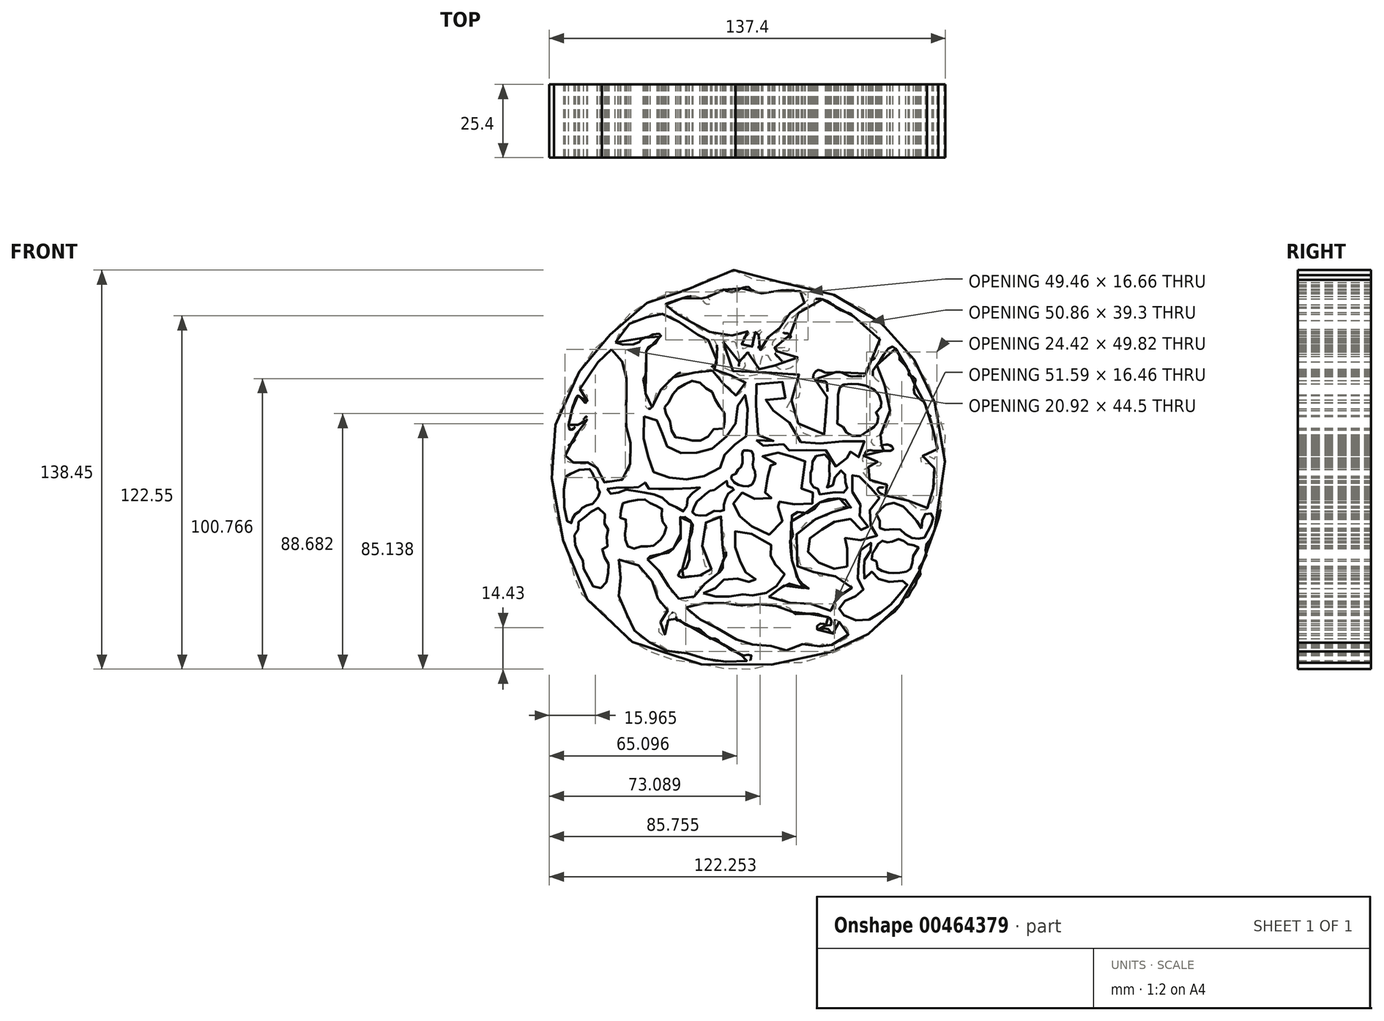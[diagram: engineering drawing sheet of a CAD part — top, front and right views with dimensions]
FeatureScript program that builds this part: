
annotation { "Feature Type Name" : "Feature", "Feature Type Description" : "" }
export const myFeature = defineFeature(function(context is Context, id is Id, definition is map)
    precondition{}
    {
        {
            var Q0;
            Q0=qCreatedBy(makeId("Front.planeOp"),FACE);
            var sketch = newSketch(context, id + "F0", { "sketchPlane" : qUnion([Q0])});
            skFitSpline(sketch, "E0", {"points": [v(-58.3, 41.66) * mm, v(-56.87, 40.83) * mm, v(-56.04, 38.93) * mm, v(-54.73, 37.5) * mm, v(-53.54, 36.31) * mm, v(-53.19, 34.05) * mm, v(-53.07, 31.2) * mm, v(-53.19, 15.04) * mm, v(-52.35, 14.2) * mm, v(-52.23, 11.47) * mm, v(-51.64, 9.21) * mm, v(-51.52, 6.96) * mm, v(-51.64, 3.75) * mm, v(-52.12, 0) * mm, v(-53.07, -2.2) * mm, v(-54.02, -3.38) * mm, v(-56.63, -3.86) * mm, v(-58.65, -3.98) * mm, v(-60.55, -4.45) * mm, v(-61.39, -4.1) * mm, v(-61.86, -2.55) * mm, v(-63.05, 0) * mm, v(-64, 1.6) * mm, v(-64.83, 2.8) * mm, v(-65.55, 3.27) * mm, v(-66.5, 2.44) * mm, v(-67.45, 1.85) * mm, v(-68.64, 1.73) * mm, v(-70.66, 2.08) * mm, v(-71.84, 2.44) * mm, v(-73.4, 2.32) * mm, v(-74.34, 2.56) * mm, v(-74.34, 4.46) * mm, v(-74.34, 6.48) * mm, v(-74.22, 8.03) * mm, v(-73.03, 8.5) * mm, v(-71.49, 9.69) * mm, v(-70.78, 10.88) * mm, v(-70.9, 12.42) * mm, v(-69.7, 13.14) * mm, v(-68.4, 13.73) * mm, v(-67.33, 15.28) * mm, v(-66.85, 16.7) * mm, v(-66.97, 18.37) * mm, v(-67.92, 17.41) * mm, v(-69.23, 15.99) * mm, v(-70.66, 15.04) * mm, v(-71.6, 13.97) * mm, v(-72.68, 13.85) * mm, v(-73.15, 15.28) * mm, v(-72.8, 17.06) * mm, v(-72.44, 18.37) * mm, v(-72.08, 20.15) * mm, v(-71.84, 21.57) * mm, v(-71.13, 23.24) * mm, v(-70.66, 24.66) * mm, v(-69.82, 25.62) * mm, v(-68.75, 24.78) * mm, v(-67.92, 23.6) * mm, v(-66.97, 23.12) * mm, v(-66.62, 25.14) * mm, v(-67.1, 26.57) * mm, v(-67.92, 27.52) * mm, v(-69.23, 28) * mm, v(-69.11, 29.18) * mm, v(-68.04, 30.01) * mm, v(-66.73, 31.68) * mm, v(-65.43, 33.46) * mm, v(-64, 35.48) * mm, v(-63.17, 36.9) * mm, v(-61.86, 38.33) * mm, v(-60.55, 39.76) * mm, v(-58.3, 41.66) * mm]});
            skFitSpline(sketch, "E1", {"points": [v(-56.85, 44.1) * mm, v(-49.42, 43.75) * mm, v(-48.22, 44.83) * mm, v(-46.66, 45.79) * mm, v(-45.1, 46.15) * mm, v(-43.42, 46.99) * mm, v(-41.03, 46.75) * mm, v(-42.23, 45.19) * mm, v(-43.3, 43.5) * mm, v(-44.74, 42.9) * mm, v(-46.06, 41.66) * mm, v(-46.18, 39.76) * mm, v(-46.18, 38.11) * mm, v(-46.18, 35.72) * mm, v(-46.66, 32.24) * mm, v(-47.26, 31.16) * mm, v(-46.9, 29.84) * mm, v(-46.66, 27.8) * mm, v(-46.42, 24.57) * mm, v(-46.42, 21.93) * mm, v(-45.46, 21.09) * mm, v(-44.5, 21.33) * mm, v(-43.66, 22.65) * mm, v(-43.18, 25.05) * mm, v(-42.7, 26.36) * mm, v(-41.27, 27.68) * mm, v(-39.83, 27.92) * mm, v(-38.99, 29) * mm, v(-38.63, 30.68) * mm, v(-36.83, 32) * mm, v(-34.8, 33.46) * mm, v(-31.68, 33.46) * mm, v(-30, 33.46) * mm, v(-27.87, 34.16) * mm, v(-26.86, 34.58) * mm, v(-25.34, 34.75) * mm, v(-23.9, 34.75) * mm, v(-22.55, 33.46) * mm, v(-21.11, 32.38) * mm, v(-20.35, 31.2) * mm, v(-20.18, 30.18) * mm, v(-19, 29.5) * mm, v(-17.56, 28.5) * mm, v(-16.46, 27.31) * mm, v(-16.04, 25.96) * mm, v(-15.2, 25.7) * mm, v(-14.1, 26.21) * mm, v(-12.74, 27.48) * mm, v(-11.9, 28.24) * mm, v(-11.73, 29.68) * mm, v(-12.07, 30.7) * mm, v(-13.67, 31.11) * mm, v(-15.2, 31.28) * mm, v(-16.3, 31.96) * mm, v(-16.89, 32.8) * mm, v(-18.58, 32.64) * mm, v(-20.6, 33.46) * mm, v(-22.1, 34.3) * mm, v(-22.53, 34.69) * mm, v(-23.01, 35.21) * mm, v(-23.45, 35.74) * mm, v(-22.48, 36.08) * mm, v(-21.81, 36.9) * mm, v(-21.86, 37.33) * mm, v(-21.76, 38.83) * mm, v(-22.11, 44.86) * mm, v(-23.16, 44.77) * mm, v(-24.65, 44.86) * mm, v(-25.6, 43.99) * mm, v(-26.05, 44.86) * mm, v(-26.05, 46.35) * mm, v(-27.62, 46.52) * mm, v(-29.28, 47.3) * mm, v(-31.11, 48.88) * mm, v(-33.9, 50.65) * mm, v(-35.06, 51.35) * mm, v(-36.36, 52.18) * mm, v(-37.78, 53.12) * mm, v(-39.31, 53.71) * mm, v(-41.08, 54.07) * mm, v(-42.73, 54.3) * mm, v(-44.74, 54.3) * mm, v(-44.86, 53.24) * mm, v(-46.63, 52.77) * mm, v(-48.04, 52.3) * mm, v(-49.34, 51.7) * mm, v(-50.87, 51.59) * mm, v(-52.4, 50.17) * mm, v(-54.06, 48.76) * mm, v(-55.6, 46.99) * mm, v(-56.85, 44.1) * mm]});
            skFitSpline(sketch, "E2", {"points": [v(-47.03, 18.43) * mm, v(-47.03, 15.19) * mm, v(-47.03, 12.58) * mm, v(-47.03, 9.21) * mm, v(-46.28, 7.85) * mm, v(-45.78, 5.98) * mm, v(-45.66, 3.36) * mm, v(-45.53, 1.12) * mm, v(-44.04, 0) * mm, v(-43.3, -1.5) * mm, v(-41.05, -2.11) * mm, v(-39.68, -2.86) * mm, v(-37.81, -2.86) * mm, v(-35.82, -3.73) * mm, v(-34.33, -3.73) * mm, v(-32.09, -3.36) * mm, v(-30.97, -2.86) * mm, v(-28.23, -2.49) * mm, v(-26.24, -2.24) * mm, v(-24.25, -2.11) * mm, v(-22.38, 0) * mm, v(-20.48, 0.65) * mm, v(-20, 1.6) * mm, v(-19.94, 2.84) * mm, v(-19.58, 4.15) * mm, v(-19, 5.1) * mm, v(-17.68, 6.23) * mm, v(-16.91, 7.18) * mm, v(-16.08, 8.2) * mm, v(-15.3, 8.73) * mm, v(-14.24, 9.62) * mm, v(-12.57, 10.33) * mm, v(-11.68, 11.05) * mm, v(-11.44, 12.17) * mm, v(-11.2, 13) * mm, v(-11.2, 14.25) * mm, v(-11.38, 15.86) * mm, v(-11.15, 16.75) * mm, v(-10.79, 18) * mm, v(-11.03, 18.77) * mm, v(-11.2, 20.61) * mm, v(-10.85, 21.45) * mm, v(-10.73, 23.05) * mm, v(-10.99, 24.42) * mm, v(-11.66, 25.7) * mm, v(-13.01, 25.7) * mm, v(-14.27, 24.8) * mm, v(-14.46, 23.94) * mm, v(-14.46, 22.1) * mm, v(-14.46, 20.37) * mm, v(-15.2, 18.15) * mm, v(-15.2, 16.03) * mm, v(-15.2, 14.17) * mm, v(-16.57, 13.18) * mm, v(-18.02, 11.73) * mm, v(-19.8, 10.27) * mm, v(-21.65, 8.75) * mm, v(-23.24, 7.43) * mm, v(-24.16, 6.7) * mm, v(-26.4, 6.11) * mm, v(-27.93, 5.91) * mm, v(-29.31, 5.85) * mm, v(-30.64, 5.85) * mm, v(-32.22, 5.78) * mm, v(-34, 5.72) * mm, v(-35.39, 5.72) * mm, v(-36.78, 6.44) * mm, v(-38.3, 7.3) * mm, v(-39.35, 8.42) * mm, v(-40.4, 9.68) * mm, v(-40.54, 10.8) * mm, v(-40.54, 11.99) * mm, v(-40.87, 12.91) * mm, v(-41.6, 13.57) * mm, v(-42.39, 15.49) * mm, v(-42.39, 16.68) * mm, v(-43.25, 18.06) * mm, v(-44.7, 18.8) * mm, v(-46.09, 18.6) * mm, v(-47.03, 18.43) * mm]});
            skFitSpline(sketch, "E3", {"points": [v(-39.87, 21.63) * mm, v(-39.75, 19.62) * mm, v(-38.45, 18.56) * mm, v(-37.74, 14.89) * mm, v(-37.14, 12.91) * mm, v(-35.96, 11.1) * mm, v(-33.48, 10.86) * mm, v(-30.64, 10.15) * mm, v(-28.62, 9.8) * mm, v(-25.9, 10.74) * mm, v(-24.25, 12.05) * mm, v(-22.23, 14.3) * mm, v(-19, 14.41) * mm, v(-19, 16.54) * mm, v(-19, 19.15) * mm, v(-20.22, 21.28) * mm, v(-22, 23.17) * mm, v(-22.7, 25.7) * mm, v(-23.65, 27.2) * mm, v(-25.2, 28.02) * mm, v(-26.85, 29.5) * mm, v(-28.98, 30.74) * mm, v(-31.1, 30.5) * mm, v(-33, 29.5) * mm, v(-35.01, 28.38) * mm, v(-36.67, 26.84) * mm, v(-37.85, 24.24) * mm, v(-39.04, 22.58) * mm, v(-39.87, 21.63) * mm]});
            skFitSpline(sketch, "E4", {"points": [v(-74, -2.4) * mm, v(-73.42, -18.32) * mm, v(-72.14, -18.44) * mm, v(-71.67, -16.58) * mm, v(-70.51, -15.18) * mm, v(-69.12, -14.25) * mm, v(-67.84, -12.74) * mm, v(-65.43, -12.16) * mm, v(-64.23, -11.23) * mm, v(-63.17, -9.72) * mm, v(-62.25, -8.2) * mm, v(-63.17, -6.23) * mm, v(-63.17, -4.02) * mm, v(-64.46, -2.62) * mm, v(-65.43, 0) * mm, v(-66.9, 0) * mm, v(-69, 0) * mm, v(-70.98, -0.88) * mm, v(-72.37, -1.46) * mm, v(-74, -2.4) * mm]});
            skFitSpline(sketch, "E5", {"points": [v(-69.78, -18.13) * mm, v(-69.78, -19.14) * mm, v(-69.82, -20.68) * mm, v(-70.4, -21.47) * mm, v(-70.92, -21.82) * mm, v(-71.18, -23.63) * mm, v(-70.96, -25.6) * mm, v(-70.61, -27.46) * mm, v(-69.86, -28.64) * mm, v(-68.97, -30.31) * mm, v(-68.2, -31.53) * mm, v(-67.98, -32.6) * mm, v(-67.98, -34.04) * mm, v(-67.52, -35.41) * mm, v(-66.38, -37.24) * mm, v(-65.43, -39.82) * mm, v(-64.1, -40.81) * mm, v(-63.17, -41.2) * mm, v(-61.44, -40.96) * mm, v(-60.55, -40.05) * mm, v(-59.91, -38.53) * mm, v(-59.61, -36.86) * mm, v(-59.3, -34.65) * mm, v(-59.15, -33.13) * mm, v(-60, -31.99) * mm, v(-60.55, -30.7) * mm, v(-61.2, -29.4) * mm, v(-61.44, -28.18) * mm, v(-61.36, -27.12) * mm, v(-60.55, -26.97) * mm, v(-59.76, -26.74) * mm, v(-59.91, -24.68) * mm, v(-59.91, -23.09) * mm, v(-59.53, -22.02) * mm, v(-59.38, -20.8) * mm, v(-59.84, -19.82) * mm, v(-60.55, -19.28) * mm, v(-60.55, -17.23) * mm, v(-60.55, -15.7) * mm, v(-61.28, -13.96) * mm, v(-63.17, -13.35) * mm, v(-64.33, -13.8) * mm, v(-65.43, -14.8) * mm, v(-66.6, -15.86) * mm, v(-68.05, -16.85) * mm, v(-69.12, -17.69) * mm, v(-69.78, -18.13) * mm]});
            skFitSpline(sketch, "E6", {"points": [v(-59.76, -6.69) * mm, v(-59.76, -8.1) * mm, v(-58.3, -8.44) * mm, v(-57.14, -8.44) * mm, v(-55.39, -7.77) * mm, v(-53.89, -7.02) * mm, v(-52.3, -7.19) * mm, v(-49.89, -7.52) * mm, v(-48.14, -7.94) * mm, v(-45.8, -8.1) * mm, v(-43.64, -8.6) * mm, v(-41.72, -9.1) * mm, v(-40.14, -10.27) * mm, v(-38.63, -11.52) * mm, v(-37.48, -12.69) * mm, v(-35.82, -13.1) * mm, v(-34.33, -13.77) * mm, v(-33.14, -14.52) * mm, v(-32.14, -13.69) * mm, v(-32.14, -12.35) * mm, v(-32.14, -10.85) * mm, v(-31.64, -9.77) * mm, v(-30.64, -8.85) * mm, v(-29.23, -7.27) * mm, v(-27.56, -6.27) * mm, v(-29.64, -6.35) * mm, v(-31.56, -6.6) * mm, v(-40.23, -6.69) * mm, v(-42.56, -6.77) * mm, v(-45.3, -6.69) * mm, v(-45.8, -5.52) * mm, v(-46.56, -4.52) * mm, v(-47.4, -5.69) * mm, v(-49.3, -6.1) * mm, v(-51.64, -6.27) * mm, v(-54.22, -6.27) * mm, v(-56.39, -6.27) * mm, v(-59.76, -6.69) * mm]});
            skFitSpline(sketch, "E7", {"points": [v(-54.38, -11.65) * mm, v(-55.05, -13.87) * mm, v(-55.05, -15.22) * mm, v(-55.18, -16.76) * mm, v(-54.1, -16.76) * mm, v(-53.03, -17.9) * mm, v(-53.03, -19.46) * mm, v(-53.57, -20.53) * mm, v(-53.5, -22.62) * mm, v(-53.43, -23.76) * mm, v(-53.43, -25.38) * mm, v(-52.56, -26.74) * mm, v(-51.35, -27.26) * mm, v(-49.6, -27.4) * mm, v(-48.05, -26.74) * mm, v(-46.9, -26.74) * mm, v(-45.36, -26.74) * mm, v(-44.35, -26.74) * mm, v(-42.33, -25.31) * mm, v(-40.87, -24.03) * mm, v(-40.18, -22.75) * mm, v(-39.5, -21.27) * mm, v(-39.37, -19.46) * mm, v(-40.18, -18.45) * mm, v(-40.87, -17.44) * mm, v(-40.87, -16.1) * mm, v(-40.87, -14.68) * mm, v(-40.87, -13.4) * mm, v(-42.47, -12.73) * mm, v(-43.81, -12.12) * mm, v(-44.89, -11.58) * mm, v(-46.23, -10.5) * mm, v(-47.1, -10.37) * mm, v(-49, -10.5) * mm, v(-51.41, -10.98) * mm, v(-52.76, -11.18) * mm, v(-54.38, -11.65) * mm]});
            skFitSpline(sketch, "E8", {"points": [v(-55.82, -31.21) * mm, v(-55.71, -32.39) * mm, v(-55.07, -33.56) * mm, v(-55.07, -36.33) * mm, v(-55.07, -37.61) * mm, v(-54.97, -39.64) * mm, v(-55.18, -41.35) * mm, v(-55.6, -42.52) * mm, v(-55.82, -44.76) * mm, v(-55.4, -45.93) * mm, v(-54.11, -47.1) * mm, v(-52.94, -50.3) * mm, v(-52.94, -52.33) * mm, v(-51.75, -53.22) * mm, v(-50.69, -55.15) * mm, v(-50.11, -56.2) * mm, v(-48.86, -57.45) * mm, v(-47.13, -58.7) * mm, v(-45.5, -59.76) * mm, v(-43.29, -60.24) * mm, v(-40.87, -60.34) * mm, v(-40.18, -61.88) * mm, v(-38.63, -63.13) * mm, v(-36.85, -63.13) * mm, v(-34.33, -63.8) * mm, v(-31.66, -63.7) * mm, v(-29.73, -64.28) * mm, v(-27.81, -65.05) * mm, v(-26.48, -65.5) * mm, v(-25.25, -65.83) * mm, v(-22.23, -66.56) * mm, v(-20.04, -66.56) * mm, v(-18.33, -66.73) * mm, v(-15.9, -66.56) * mm, v(-13.67, -66.56) * mm, v(-11.66, -66.32) * mm, v(-10.2, -66.32) * mm, v(-9.95, -64.2) * mm, v(-11.9, -64.53) * mm, v(-13.67, -64.12) * mm, v(-15.2, -63.3) * mm, v(-16.95, -62.5) * mm, v(-19, -61.03) * mm, v(-21.02, -59.64) * mm, v(-21.76, -58.75) * mm, v(-24.25, -58.67) * mm, v(-25.17, -57.69) * mm, v(-26.88, -56.22) * mm, v(-28.1, -55.25) * mm, v(-29.49, -54.92) * mm, v(-32.01, -54.1) * mm, v(-33.64, -53.21) * mm, v(-34.33, -52.32) * mm, v(-35.82, -52.23) * mm, v(-35.82, -50.36) * mm, v(-36.9, -49.63) * mm, v(-37.87, -50.04) * mm, v(-38.63, -51.58) * mm, v(-38.63, -53.37) * mm, v(-39.42, -53.86) * mm, v(-39.58, -55.16) * mm, v(-39.5, -56.71) * mm, v(-40.18, -57.44) * mm, v(-41.7, -57.04) * mm, v(-41.7, -55.16) * mm, v(-41.62, -53.62) * mm, v(-40.87, -52.56) * mm, v(-40.18, -51.99) * mm, v(-40.18, -50.69) * mm, v(-40.18, -49.38) * mm, v(-38.63, -48.73) * mm, v(-38.63, -47.6) * mm, v(-40.18, -46.86) * mm, v(-41.54, -46.3) * mm, v(-42.19, -44.58) * mm, v(-42.27, -42.8) * mm, v(-42.68, -41.08) * mm, v(-43.65, -39.45) * mm, v(-45.12, -37.99) * mm, v(-46.83, -36.52) * mm, v(-48.21, -34.32) * mm, v(-49.27, -32.94) * mm, v(-51.06, -31.8) * mm, v(-52.94, -31.72) * mm, v(-55.82, -31.21) * mm]});
            skFitSpline(sketch, "E9", {"points": [v(-45.81, -31.07) * mm, v(-44.91, -32.27) * mm, v(-43.36, -33.53) * mm, v(-42.52, -34.55) * mm, v(-40.87, -35.99) * mm, v(-40.18, -37.79) * mm, v(-38.63, -40.12) * mm, v(-37.84, -42.16) * mm, v(-35.82, -43.42) * mm, v(-35.26, -44.5) * mm, v(-33.7, -45.34) * mm, v(-31.79, -45.46) * mm, v(-30.1, -44.56) * mm, v(-29.33, -43.3) * mm, v(-28.9, -41.62) * mm, v(-27.35, -40.54) * mm, v(-25.13, -38.99) * mm, v(-24.25, -38.09) * mm, v(-22.23, -36.77) * mm, v(-20.7, -35.5) * mm, v(-19.68, -33.9) * mm, v(-19.68, -31.67) * mm, v(-19, -30.65) * mm, v(-18.54, -29.15) * mm, v(-19, -27.18) * mm, v(-19.62, -26.74) * mm, v(-19.62, -24.3) * mm, v(-19, -22.68) * mm, v(-19.62, -21.48) * mm, v(-20.1, -20.64) * mm, v(-20.34, -18.45) * mm, v(-19.74, -17.59) * mm, v(-19.74, -16.57) * mm, v(-20.82, -16.39) * mm, v(-21.76, -16.5) * mm, v(-24.25, -17.53) * mm, v(-25.55, -18.45) * mm, v(-25.31, -20.34) * mm, v(-26.27, -21.84) * mm, v(-26.15, -32.63) * mm, v(-24.95, -34.2) * mm, v(-23.57, -34.6) * mm, v(-23.57, -36.1) * mm, v(-24.25, -36.59) * mm, v(-26.81, -36.65) * mm, v(-29.39, -36.95) * mm, v(-31.07, -36.95) * mm, v(-31.9, -37.3) * mm, v(-34.33, -37.55) * mm, v(-34.9, -37.55) * mm, v(-35.14, -35.69) * mm, v(-34.33, -35.03) * mm, v(-32.75, -34.25) * mm, v(-31.43, -33.17) * mm, v(-31.07, -22.08) * mm, v(-30.17, -21.42) * mm, v(-30.17, -18.96) * mm, v(-31, -17.77) * mm, v(-31.9, -16.93) * mm, v(-33.05, -16.39) * mm, v(-34.33, -16.33) * mm, v(-34.33, -18.45) * mm, v(-34.33, -19.74) * mm, v(-34.33, -21.24) * mm, v(-34.33, -24.18) * mm, v(-35.14, -24.96) * mm, v(-36.4, -26.74) * mm, v(-37.36, -28.14) * mm, v(-38.63, -28.92) * mm, v(-40.18, -29.1) * mm, v(-40.87, -29.27) * mm, v(-42.82, -29.7) * mm, v(-44.8, -30.05) * mm, v(-45.51, -30.35) * mm, v(-45.81, -31.07) * mm]});
            skFitSpline(sketch, "E10", {"points": [v(-32.56, -47.89) * mm, v(-30.67, -49.78) * mm, v(-28.67, -51.47) * mm, v(-25.93, -52.52) * mm, v(-24.25, -52.94) * mm, v(-21.76, -54.94) * mm, v(-19, -56.71) * mm, v(-15.2, -58.73) * mm, v(-13.67, -60.3) * mm, v(-10.77, -60.52) * mm, v(-9.2, -60.73) * mm, v(-6.25, -61.05) * mm, v(-3.82, -61.05) * mm, v(-1.61, -61.78) * mm, v(0, -62.62) * mm, v(1.97, -63.05) * mm, v(3.44, -61.68) * mm, v(5.65, -61.89) * mm, v(8.5, -60.3) * mm, v(11.13, -60.3) * mm, v(13.02, -61.15) * mm, v(14.81, -61.15) * mm, v(15.13, -60.1) * mm, v(16.7, -60.94) * mm, v(18.92, -60.52) * mm, v(22.07, -59.15) * mm, v(23.86, -57.47) * mm, v(23.55, -55.36) * mm, v(22.18, -54.2) * mm, v(20.6, -52.83) * mm, v(19.13, -52.3) * mm, v(19.13, -56.71) * mm, v(18.18, -56.71) * mm, v(16.5, -55.15) * mm, v(14.7, -55.36) * mm, v(13.02, -55.47) * mm, v(13.34, -53.89) * mm, v(14.92, -53.47) * mm, v(16.28, -54) * mm, v(17.86, -53.89) * mm, v(17.86, -52.1) * mm, v(17.23, -51.36) * mm, v(15.02, -50.83) * mm, v(11.97, -49.89) * mm, v(9.13, -50.1) * mm, v(6.6, -50.1) * mm, v(5.23, -50.1) * mm, v(3.97, -48.52) * mm, v(2.28, -47.68) * mm, v(-0.88, -47.36) * mm, v(-2.14, -47.36) * mm, v(-4.98, -46.41) * mm, v(-7.72, -46.94) * mm, v(-10.14, -47.68) * mm, v(-13.67, -47.36) * mm, v(-15.2, -46.1) * mm, v(-17.5, -45.89) * mm, v(-19, -46.3) * mm, v(-21.76, -46.3) * mm, v(-24.25, -46.3) * mm, v(-27.2, -46.52) * mm, v(-29.83, -46.94) * mm, v(-32.56, -47.89) * mm]});
            skFitSpline(sketch, "E11", {"points": [v(-26.42, -42.99) * mm, v(-24.25, -42) * mm, v(-22.23, -41.03) * mm, v(-22.23, -40.05) * mm, v(-19, -38.1) * mm, v(-17.12, -37.97) * mm, v(-13.67, -37.85) * mm, v(-11.86, -38.34) * mm, v(-10.14, -39.2) * mm, v(-7.7, -39.32) * mm, v(-8.92, -37.48) * mm, v(-10.14, -36.75) * mm, v(-12.23, -35.28) * mm, v(-13.67, -33.93) * mm, v(-13.67, -30.65) * mm, v(-15.2, -27.7) * mm, v(-15.2, -23.66) * mm, v(-15.2, -21.09) * mm, v(-13.67, -20.35) * mm, v(-13.67, -21.58) * mm, v(-11.74, -22.31) * mm, v(-10.14, -22.31) * mm, v(-8.07, -22.92) * mm, v(-6.72, -23.9) * mm, v(-5, -24.88) * mm, v(-4.03, -25.25) * mm, v(-2.44, -26.74) * mm, v(-2.2, -28.18) * mm, v(-3.3, -30.65) * mm, v(-2.68, -31.98) * mm, v(-1.34, -33.08) * mm, v(0.86, -34.67) * mm, v(1.72, -36.87) * mm, v(0, -39.56) * mm, v(-1.95, -40.9) * mm, v(-3.42, -42) * mm, v(-6.6, -43.6) * mm, v(-9.17, -43.72) * mm, v(-10.14, -43.72) * mm, v(-11.62, -42.99) * mm, v(-13.67, -43.72) * mm, v(-16.5, -44.09) * mm, v(-19, -44.09) * mm, v(-21.76, -44.09) * mm, v(-24.25, -44.09) * mm, v(-26.42, -42.99) * mm]});
            skFitSpline(sketch, "E12", {"points": [v(-3.65, -44.25) * mm, v(-1.62, -42.43) * mm, v(0, -41.52) * mm, v(1.1, -40.6) * mm, v(2.63, -39.7) * mm, v(4.65, -39.8) * mm, v(7.59, -40.91) * mm, v(10.22, -41.22) * mm, v(8.2, -39.9) * mm, v(6.68, -38.38) * mm, v(5.77, -36.66) * mm, v(5.26, -34.53) * mm, v(4.55, -32.3) * mm, v(4.05, -29.78) * mm, v(3.84, -27.35) * mm, v(3.84, -24.2) * mm, v(4.65, -23.6) * mm, v(4.45, -21.98) * mm, v(4.25, -20.26) * mm, v(4.25, -16.1) * mm, v(5.46, -14.59) * mm, v(7.59, -15.2) * mm, v(10.02, -15) * mm, v(12.25, -13.58) * mm, v(13.36, -12.16) * mm, v(14.58, -11.04) * mm, v(17.41, -10.23) * mm, v(19.64, -10.03) * mm, v(21.66, -10.13) * mm, v(23.59, -11.15) * mm, v(24.8, -13.17) * mm, v(23.69, -13.17) * mm, v(20.55, -13.17) * mm, v(19.23, -13.47) * mm, v(18.63, -14.28) * mm, v(17.1, -15.6) * mm, v(15.39, -16.61) * mm, v(13.66, -16.92) * mm, v(11.74, -17.42) * mm, v(8.4, -19.04) * mm, v(6.17, -22.08) * mm, v(5.16, -24.2) * mm, v(4.96, -26.74) * mm, v(6.07, -29.37) * mm, v(7.29, -30.38) * mm, v(7.7, -31.9) * mm, v(5.87, -33.02) * mm, v(6.98, -33.83) * mm, v(8.9, -33.62) * mm, v(10.63, -33.93) * mm, v(12.15, -35.85) * mm, v(14.47, -36.86) * mm, v(17.92, -36.86) * mm, v(21.36, -37.57) * mm, v(24.5, -38.69) * mm, v(25.2, -40.5) * mm, v(24.2, -42.23) * mm, v(22.78, -42.94) * mm, v(20.75, -43.55) * mm, v(19.44, -45.67) * mm, v(19.33, -47.2) * mm, v(19.33, -48.5) * mm, v(17.82, -49.01) * mm, v(17.41, -49.01) * mm, v(14.88, -47.8) * mm, v(11.94, -46.68) * mm, v(9.2, -46.68) * mm, v(6.88, -46.38) * mm, v(4.05, -46.38) * mm, v(1.72, -45.17) * mm, v(0, -44.96) * mm, v(-3.65, -44.25) * mm]});
            skFitSpline(sketch, "E13", {"points": [v(22.77, -45.6) * mm, v(21.94, -47.02) * mm, v(20.95, -47.51) * mm, v(20.62, -49.26) * mm, v(20.7, -50.5) * mm, v(22.52, -50.5) * mm, v(24.27, -51.66) * mm, v(26.84, -52.4) * mm, v(29.5, -52.74) * mm, v(31.23, -52) * mm, v(33.64, -50.67) * mm, v(35.38, -49.42) * mm, v(37.2, -48.43) * mm, v(38.78, -46.68) * mm, v(40.36, -45.44) * mm, v(41.69, -43.2) * mm, v(43.35, -41.7) * mm, v(44.42, -39.8) * mm, v(44.6, -38.3) * mm, v(43.35, -38.39) * mm, v(41.69, -39.05) * mm, v(39.12, -39.14) * mm, v(36.7, -38.8) * mm, v(35.38, -38.55) * mm, v(33.97, -37.64) * mm, v(32.98, -36.56) * mm, v(32.31, -35.73) * mm, v(31.15, -35.24) * mm, v(29.82, -36.65) * mm, v(29.33, -37.9) * mm, v(28.58, -36.48) * mm, v(29.33, -34.4) * mm, v(30.07, -33.9) * mm, v(29.33, -32.5) * mm, v(29.58, -31.17) * mm, v(30.32, -29.6) * mm, v(31.57, -28.27) * mm, v(32.31, -26.6) * mm, v(32.31, -25.36) * mm, v(30.49, -26.2) * mm, v(28.75, -27.52) * mm, v(27.75, -28.52) * mm, v(27.42, -31.67) * mm, v(27.34, -34.08) * mm, v(27.17, -36.73) * mm, v(27.25, -38.72) * mm, v(28.41, -40.46) * mm, v(29.08, -42.62) * mm, v(27.58, -43.28) * mm, v(26, -44.11) * mm, v(24.35, -44.36) * mm, v(22.77, -45.6) * mm]});
            skFitSpline(sketch, "E14", {"points": [v(39.53, -35.88) * mm, v(41.54, -35.8) * mm, v(43.86, -35.5) * mm, v(44.87, -34.96) * mm, v(45.88, -33.64) * mm, v(46.18, -31.55) * mm, v(46.57, -29.54) * mm, v(47.42, -28.38) * mm, v(48.04, -27.52) * mm, v(48.04, -26.36) * mm, v(45.41, -26.36) * mm, v(44.25, -25.67) * mm, v(43.01, -24.82) * mm, v(41.93, -24.2) * mm, v(39.68, -24.66) * mm, v(38.37, -25.43) * mm, v(36.97, -25.05) * mm, v(35.66, -24.74) * mm, v(34.5, -25.51) * mm, v(33.8, -26.44) * mm, v(32.8, -28.3) * mm, v(32.18, -29.15) * mm, v(31.94, -31.09) * mm, v(33.34, -31.47) * mm, v(33.88, -33.8) * mm, v(34.5, -34.96) * mm, v(36.59, -35.34) * mm, v(38.29, -35.96) * mm, v(39.53, -35.88) * mm]});
            skFitSpline(sketch, "E15", {"points": [v(23.5, -33.69) * mm, v(22.07, -34.26) * mm, v(20.17, -34.45) * mm, v(19.12, -34.45) * mm, v(17.22, -34.35) * mm, v(14.56, -32.55) * mm, v(12.94, -32.17) * mm, v(10.76, -30.84) * mm, v(10.19, -29.03) * mm, v(9.05, -27.04) * mm, v(9.43, -25.42) * mm, v(10.66, -23.71) * mm, v(11.8, -22) * mm, v(13.04, -20.86) * mm, v(15.98, -20.67) * mm, v(17.22, -19.53) * mm, v(18.27, -18.86) * mm, v(20.36, -17.25) * mm, v(21.36, -17.25) * mm, v(24.63, -17.15) * mm, v(26.25, -17.82) * mm, v(27.3, -19.53) * mm, v(28.62, -21.15) * mm, v(29.29, -21.15) * mm, v(30.9, -21.15) * mm, v(31, -20) * mm, v(29.57, -19.63) * mm, v(28.34, -18.3) * mm, v(27.86, -16.2) * mm, v(27.3, -15.25) * mm, v(28.43, -14.02) * mm, v(28.24, -12.5) * mm, v(27.39, -11.07) * mm, v(26.44, -9.65) * mm, v(25.3, -7.56) * mm, v(25.68, -4.7) * mm, v(25.4, -2.9) * mm, v(25.4, -0.9) * mm, v(26.06, 0) * mm, v(27.2, -1.67) * mm, v(28.34, -3.47) * mm, v(29.67, -4.7) * mm, v(31.95, -6.6) * mm, v(33.37, -7.84) * mm, v(34.42, -9.08) * mm, v(34.7, -9.84) * mm, v(33.18, -10.7) * mm, v(31.85, -12.5) * mm, v(31.19, -14.68) * mm, v(31.19, -16.77) * mm, v(31.28, -18.58) * mm, v(32.04, -20.2) * mm, v(32.8, -21.24) * mm, v(33.85, -22.29) * mm, v(33.56, -23.24) * mm, v(31.1, -23.9) * mm, v(28.62, -24.47) * mm, v(25.49, -24.76) * mm, v(23.97, -24.38) * mm, v(22.64, -23.8) * mm, v(21.36, -25.33) * mm, v(22.64, -26.66) * mm, v(23.78, -27.9) * mm, v(24.06, -30.46) * mm, v(23.5, -33.69) * mm]});
            skFitSpline(sketch, "E16", {"points": [v(49.22, -20.4) * mm, v(49.58, -17.6) * mm, v(50.3, -15.54) * mm, v(51.76, -15.42) * mm, v(53.1, -15.3) * mm, v(53.34, -17.12) * mm, v(52.61, -19.3) * mm, v(51.64, -21.12) * mm, v(50.55, -23.18) * mm, v(49.58, -23.91) * mm, v(47.64, -23.91) * mm, v(45.94, -23.8) * mm, v(43.76, -22.58) * mm, v(42.18, -20.88) * mm, v(40.48, -20.76) * mm, v(37.82, -20.76) * mm, v(35.4, -21) * mm, v(34.78, -19.9) * mm, v(34.78, -17.85) * mm, v(33.7, -15.42) * mm, v(35.03, -13.85) * mm, v(36.36, -12.51) * mm, v(38.06, -11.9) * mm, v(41.58, -11.9) * mm, v(46.06, -16.15) * mm, v(47.52, -17.73) * mm, v(49.22, -20.4) * mm]});
            skFitSpline(sketch, "E17", {"points": [v(-22.67, -7.13) * mm, v(-23.77, -7.25) * mm, v(-25.6, -8.47) * mm, v(-27.06, -9.81) * mm, v(-28.53, -11.03) * mm, v(-29.75, -13.36) * mm, v(-30.12, -15.07) * mm, v(-29.02, -15.8) * mm, v(-27.3, -16.04) * mm, v(-25.23, -15.8) * mm, v(-24.38, -15.31) * mm, v(-22.79, -14.46) * mm, v(-20.83, -14.46) * mm, v(-19.37, -14.33) * mm, v(-19.37, -12.62) * mm, v(-18.64, -10.06) * mm, v(-17.66, -8.23) * mm, v(-15.58, -6.76) * mm, v(-16.31, -6.4) * mm, v(-18.02, -5.66) * mm, v(-18.27, -3.95) * mm, v(-19.61, -4.93) * mm, v(-20.83, -5.78) * mm, v(-22.67, -7.13) * mm]});
            skFitSpline(sketch, "E18", {"points": [v(-10.94, 6.56) * mm, v(-9.6, 6.31) * mm, v(-9.1, 4.97) * mm, v(-9.1, 2.65) * mm, v(-9.23, 1.06) * mm, v(-8.74, 0) * mm, v(-8.37, -2.24) * mm, v(-8.86, -4.07) * mm, v(-10.2, -5.66) * mm, v(-12.4, -5.78) * mm, v(-14.48, -5.17) * mm, v(-16.31, -3.83) * mm, v(-16.8, -2.24) * mm, v(-15.46, -1.75) * mm, v(-14.36, 0) * mm, v(-13.14, 1.18) * mm, v(-12.9, 3.14) * mm, v(-12.9, 5.1) * mm, v(-12.77, 6.43) * mm, v(-10.94, 6.56) * mm]});
            skFitSpline(sketch, "E19", {"points": [v(-13.02, -7.98) * mm, v(-14.73, -8.47) * mm, v(-15.58, -10.67) * mm, v(-16.31, -12.62) * mm, v(-16.07, -14.46) * mm, v(-13.87, -16.04) * mm, v(-12.4, -17.75) * mm, v(-11.06, -18.85) * mm, v(-8.86, -20.2) * mm, v(-5.69, -21.66) * mm, v(-2.88, -22.76) * mm, v(0, -22.15) * mm, v(1.15, -14.7) * mm, v(1.15, -13.11) * mm, v(0, -12.99) * mm, v(-2.39, -12.13) * mm, v(-1.41, -11.16) * mm, v(0, -11.16) * mm, v(2.38, -11.28) * mm, v(3.72, -11.77) * mm, v(5.92, -12.13) * mm, v(9.46, -12.74) * mm, v(11.66, -11.52) * mm, v(12.64, -9.57) * mm, v(11.54, -9.57) * mm, v(11.54, -7.13) * mm, v(9.58, -7.13) * mm, v(7.87, -7.13) * mm, v(7.87, -5.78) * mm, v(8.73, -5.17) * mm, v(8.36, -2.48) * mm, v(8.12, 0) * mm, v(8.24, 2.04) * mm, v(8.85, 2.65) * mm, v(8.6, 3.87) * mm, v(6.28, 3.87) * mm, v(4.09, 4.72) * mm, v(2, 5.95) * mm, v(0, 5.95) * mm, v(-1.66, 5.7) * mm, v(-6.05, 5.7) * mm, v(-5.2, 3.38) * mm, v(-4.59, 2.77) * mm, v(-2.39, 2.9) * mm, v(0, 0) * mm, v(-2.02, 1.18) * mm, v(-3.37, 1.43) * mm, v(-3.85, 1.3) * mm, v(-3.85, 0) * mm, v(-4.1, -2.48) * mm, v(-6.18, -5.42) * mm, v(-5.2, -7.86) * mm, v(-3.12, -8.6) * mm, v(-1.53, -9.7) * mm, v(-3.24, -9.94) * mm, v(-5.44, -10.06) * mm, v(-8.13, -10.18) * mm, v(-9.96, -10.18) * mm, v(-11.67, -9.2) * mm, v(-13.02, -7.98) * mm]});
            skFitSpline(sketch, "E20", {"points": [v(10.8, -4.51) * mm, v(10.9, -2.26) * mm, v(10.72, 0.77) * mm, v(11.41, 0) * mm, v(11.5, 2.06) * mm, v(11.76, 3.97) * mm, v(13.14, 4.83) * mm, v(15.39, 5.18) * mm, v(16.86, 4.74) * mm, v(17.38, 2.15) * mm, v(17.2, 0) * mm, v(17.38, -1.14) * mm, v(17.47, -2.95) * mm, v(17.2, -4.77) * mm, v(16, -5.2) * mm, v(16.43, -6.15) * mm, v(17.98, -6.15) * mm, v(18.68, -4.86) * mm, v(19.2, -2.95) * mm, v(19.71, -1.66) * mm, v(22.57, 0) * mm, v(22.66, -2.35) * mm, v(22.74, -4.17) * mm, v(23.17, -4.94) * mm, v(23.43, -6.07) * mm, v(23.6, -7.13) * mm, v(22.4, -7.97) * mm, v(20.32, -7.8) * mm, v(18.16, -8.14) * mm, v(16.6, -8.23) * mm, v(14.78, -8.32) * mm, v(13.4, -8.58) * mm, v(13.31, -7.13) * mm, v(13.23, -6.07) * mm, v(12.1, -6.07) * mm, v(11.06, -5.9) * mm, v(10.8, -4.51) * mm]});
            skPoint(sketch, "E21.13.internal.snap0", {"position": v(64.71, -3) * mm});
            skPoint(sketch, "E21.78.internal.snap0", {"position": v(64.71, -3) * mm});
            skFitSpline(sketch, "E21", {"points": [v(36.68, -9.04) * mm, v(38.29, -8.92) * mm, v(41.69, -9.29) * mm, v(43.76, -10.26) * mm, v(45.23, -11.28) * mm, v(47.06, -13.07) * mm, v(48.65, -14.17) * mm, v(50.85, -13.93) * mm, v(52.8, -11.28) * mm, v(53.29, -11.28) * mm, v(53.41, -8.92) * mm, v(53.29, -7.13) * mm, v(54.02, -4.89) * mm, v(54.76, -3) * mm, v(54.51, -1.75) * mm, v(53.9, 0) * mm, v(52.43, 1.95) * mm, v(49.26, 2.2) * mm, v(48.77, 3.42) * mm, v(49.75, 4.72) * mm, v(51.58, 4.72) * mm, v(53.78, 3.66) * mm, v(54.63, 4.72) * mm, v(54.63, 7.94) * mm, v(53.53, 9.28) * mm, v(53.05, 10.63) * mm, v(53.05, 13.07) * mm, v(53.05, 16.12) * mm, v(52.68, 18.08) * mm, v(51.82, 18.81) * mm, v(50.36, 23.09) * mm, v(49.5, 23.82) * mm, v(46.82, 26.39) * mm, v(46.57, 27.85) * mm, v(47.08, 30.41) * mm, v(46.93, 32) * mm, v(44.9, 32.59) * mm, v(45.05, 34.18) * mm, v(43.76, 35.92) * mm, v(43.76, 36.06) * mm, v(41.69, 37.94) * mm, v(41.69, 39.54) * mm, v(39.84, 42.3) * mm, v(38.29, 42.44) * mm, v(35.64, 38.96) * mm, v(33.6, 36.06) * mm, v(32.16, 33.3) * mm, v(33.46, 31.28) * mm, v(36.07, 29.54) * mm, v(38.29, 27.52) * mm, v(38.29, 26.07) * mm, v(38.29, 21.58) * mm, v(38.29, 17.81) * mm, v(36.5, 14.04) * mm, v(35.92, 12.74) * mm, v(33.75, 11.44) * mm, v(31.72, 10.13) * mm, v(32.74, 8.4) * mm, v(35.5, 8.4) * mm, v(38.29, 8.4) * mm, v(39.4, 7.1) * mm, v(38.29, 6.51) * mm, v(35.78, 6.51) * mm, v(34.33, 6.51) * mm, v(32.74, 6.51) * mm, v(30.57, 6.51) * mm, v(28.68, 3.32) * mm, v(29.4, 2.02) * mm, v(30.71, 2.31) * mm, v(33.17, 2.31) * mm, v(34.77, 2.75) * mm, v(35.35, 1.73) * mm, v(33.67, 1.15) * mm, v(31.79, 1.15) * mm, v(31.02, 0.98) * mm, v(29.57, 0) * mm, v(28.71, 0) * mm, v(29.4, -1.75) * mm, v(30.85, -3) * mm, v(31.96, -4.23) * mm, v(33.58, -4.65) * mm, v(34.86, -4.57) * mm, v(36.4, -4.57) * mm, v(37.34, -5.5) * mm, v(35.97, -6.2) * mm, v(34.6, -6.28) * mm, v(34, -7.13) * mm, v(36.68, -9.04) * mm]});
            skFitSpline(sketch, "E22", {"points": [v(-7.95, 10.1) * mm, v(-6.86, 9.76) * mm, v(-5.42, 9.42) * mm, v(-4.4, 9.42) * mm, v(-2.14, 9.5) * mm, v(-2.14, 9.97) * mm, v(-3.58, 9.97) * mm, v(-4.53, 10.04) * mm, v(-5.5, 10.31) * mm, v(-6.72, 11.06) * mm, v(-7.4, 11.88) * mm, v(-7.75, 14.62) * mm, v(-7.54, 15.99) * mm, v(-8.02, 21.45) * mm, v(-8.5, 23.85) * mm, v(-8.5, 24.6) * mm, v(-8.64, 28.02) * mm, v(-8.43, 29.18) * mm, v(-5.97, 30.68) * mm, v(-2.76, 30.82) * mm, v(-0.57, 30.55) * mm, v(1.96, 30) * mm, v(3.2, 28.36) * mm, v(4.01, 26.65) * mm, v(2.85, 25.56) * mm, v(1.34, 24.19) * mm, v(0, 23.64) * mm, v(-2.55, 23.3) * mm, v(-3.44, 23.57) * mm, v(-4.94, 24.12) * mm, v(-5.56, 22.82) * mm, v(-6.1, 21.18) * mm, v(-4.74, 20.5) * mm, v(-1.87, 20.5) * mm, v(-0.91, 20.22) * mm, v(0.6, 19.34) * mm, v(2.58, 17.35) * mm, v(3.26, 16.53) * mm, v(4.35, 14.76) * mm, v(4.83, 13.93) * mm, v(6, 11.95) * mm, v(7.16, 9.76) * mm, v(8.66, 8.88) * mm, v(10.23, 8.26) * mm, v(12, 8.88) * mm, v(13.3, 9.01) * mm, v(15.5, 9.08) * mm, v(17.82, 9.42) * mm, v(19.19, 10.38) * mm, v(21.58, 9.9) * mm, v(23.08, 9.08) * mm, v(25.54, 9.5) * mm, v(28.42, 9.9) * mm, v(29.17, 9.9) * mm, v(30.8, 8.6) * mm, v(29.92, 7.78) * mm, v(28.62, 6.14) * mm, v(27.6, 4.98) * mm, v(26.84, 2.18) * mm, v(25, 1.9) * mm, v(25, 3) * mm, v(24.59, 6.14) * mm, v(24.66, 7.99) * mm, v(23.08, 7.1) * mm, v(23.08, 5.6) * mm, v(23.29, 4.3) * mm, v(23.5, 3.4) * mm, v(23.43, 1.9) * mm, v(22.33, 1.22) * mm, v(21.44, 1.22) * mm, v(20.08, 1.22) * mm, v(19.12, 1.15) * mm, v(18.91, 4.57) * mm, v(18.37, 6) * mm, v(16.66, 6.21) * mm, v(15.77, 7.1) * mm, v(14.13, 7.1) * mm, v(12.21, 6.9) * mm, v(11.53, 6.83) * mm, v(9.27, 6.69) * mm, v(7.84, 7.03) * mm, v(6.27, 7.37) * mm, v(5.65, 6.21) * mm, v(3.94, 6.28) * mm, v(2.99, 7.3) * mm, v(3.6, 8.8) * mm, v(3.67, 10.31) * mm, v(2.17, 9.63) * mm, v(1.2, 8.6) * mm, v(0, 8.26) * mm, v(-1.18, 8.26) * mm, v(-3.58, 8.12) * mm, v(-5.22, 8.2) * mm, v(-7.47, 8.33) * mm, v(-8.98, 8.33) * mm, v(-9.52, 9.15) * mm, v(-8.84, 9.97) * mm, v(-7.95, 10.1) * mm]});
            skFitSpline(sketch, "E23", {"points": [v(-39.5, 57.14) * mm, v(-38.67, 56.06) * mm, v(-37.68, 56.4) * mm, v(-36.44, 55.65) * mm, v(-35.62, 53.92) * mm, v(-33.72, 53.84) * mm, v(-31.82, 52.27) * mm, v(-30.59, 51.11) * mm, v(-28.69, 49.63) * mm, v(-25.64, 47.9) * mm, v(-24.32, 47.82) * mm, v(-22.26, 46.9) * mm, v(-18.54, 46.25) * mm, v(-15.99, 46.66) * mm, v(-14.42, 46.9) * mm, v(-12.52, 47.32) * mm, v(-11.45, 48.06) * mm, v(-10.7, 47.07) * mm, v(-12.03, 46.33) * mm, v(-12.6, 45.34) * mm, v(-13.02, 43.7) * mm, v(-12.94, 42.04) * mm, v(-12.11, 42.04) * mm, v(-10.87, 42.7) * mm, v(-10.05, 42.7) * mm, v(-8.98, 42.78) * mm, v(-9.14, 44.68) * mm, v(-9.22, 47.65) * mm, v(-8.15, 47.65) * mm, v(-6.42, 48.48) * mm, v(-5.68, 48.64) * mm, v(-6.09, 47.9) * mm, v(-7.24, 46.66) * mm, v(-7.4, 44.68) * mm, v(-7.16, 43.03) * mm, v(-7.16, 41.63) * mm, v(-6.42, 41.46) * mm, v(-5.18, 42.12) * mm, v(-4.6, 43.7) * mm, v(-4.11, 45.26) * mm, v(-3.2, 46.74) * mm, v(-2.21, 46.9) * mm, v(0, 48.31) * mm, v(0, 48.89) * mm, v(0.6, 49.88) * mm, v(0.92, 51.77) * mm, v(2.4, 53.34) * mm, v(4.47, 54.74) * mm, v(5.79, 55.49) * mm, v(7.27, 56.64) * mm, v(8.6, 57.71) * mm, v(9.91, 59.03) * mm, v(9.75, 59.94) * mm, v(8.5, 61.01) * mm, v(6.78, 62.08) * mm, v(5.54, 62.41) * mm, v(4.06, 62.41) * mm, v(1.42, 62.25) * mm, v(-1.06, 62) * mm, v(-3.37, 61.1) * mm, v(-6.42, 61.18) * mm, v(-9.55, 62.25) * mm, v(-11.04, 63.32) * mm, v(-14.34, 62.33) * mm, v(-15.74, 61.67) * mm, v(-18.3, 61.92) * mm, v(-19.29, 62.41) * mm, v(-22.59, 61.75) * mm, v(-23.99, 60.6) * mm, v(-25.06, 60.02) * mm, v(-23.82, 58.13) * mm, v(-25.06, 57.22) * mm, v(-26.54, 58.62) * mm, v(-27.86, 59.7) * mm, v(-30.1, 60.1) * mm, v(-32.4, 59.77) * mm, v(-34.46, 59.11) * mm, v(-36.94, 58.37) * mm, v(-38.83, 57.71) * mm, v(-39.5, 57.14) * mm]});
            skFitSpline(sketch, "E24", {"points": [v(-19.54, 44.28) * mm, v(-19.2, 39.8) * mm, v(-19.2, 37.22) * mm, v(-19.2, 34.38) * mm, v(-17.22, 34.38) * mm, v(-14.78, 33.39) * mm, v(-13.6, 32.73) * mm, v(-11.48, 32.53) * mm, v(-9.37, 32.46) * mm, v(-5.4, 33.45) * mm, v(-2.37, 33.59) * mm, v(0, 33) * mm, v(2.65, 33.26) * mm, v(5.03, 33.39) * mm, v(6.75, 33) * mm, v(6.28, 31.67) * mm, v(6.75, 29.03) * mm, v(7.67, 26.85) * mm, v(6.42, 24.87) * mm, v(4.37, 24.08) * mm, v(3.18, 23.15) * mm, v(2, 21.44) * mm, v(3.77, 20.97) * mm, v(5.1, 19.78) * mm, v(6.02, 16.88) * mm, v(7.6, 14.37) * mm, v(8.33, 12.52) * mm, v(10.58, 11.13) * mm, v(14.34, 12.06) * mm, v(15.33, 12) * mm, v(16.12, 14.83) * mm, v(16.25, 19.06) * mm, v(16.72, 22.23) * mm, v(16.52, 24.54) * mm, v(16.52, 25.46) * mm, v(16.65, 27.05) * mm, v(16.65, 27.38) * mm, v(16.52, 29.62) * mm, v(16.12, 30.55) * mm, v(14.27, 30.81) * mm, v(12.42, 31.2) * mm, v(11.63, 32) * mm, v(12.5, 34.05) * mm, v(13.74, 34.5) * mm, v(15.92, 33.65) * mm, v(18.37, 33.59) * mm, v(20.67, 33.78) * mm, v(22.03, 33.5) * mm, v(23.78, 32.52) * mm, v(26.5, 32.33) * mm, v(29.7, 32.62) * mm, v(30, 33.69) * mm, v(30.67, 36.4) * mm, v(33.68, 39.42) * mm, v(34.75, 43.6) * mm, v(34.85, 44.95) * mm, v(34.36, 46.8) * mm, v(32.23, 48.93) * mm, v(30.41, 50.15) * mm, v(27.66, 51.46) * mm, v(24.8, 53.85) * mm, v(22.64, 54.69) * mm, v(19.9, 56.12) * mm, v(17.5, 57.8) * mm, v(15.11, 59) * mm, v(13.44, 59.23) * mm, v(12, 58.87) * mm, v(12.12, 56.72) * mm, v(8.9, 56.12) * mm, v(6.74, 54.45) * mm, v(3.87, 52.18) * mm, v(2.92, 50.98) * mm, v(1.36, 48.6) * mm, v(1.48, 47.4) * mm, v(3.28, 47.04) * mm, v(3.87, 45.84) * mm, v(1.96, 45.48) * mm, v(0, 45.6) * mm, v(-1.39, 45.25) * mm, v(-2.58, 43.81) * mm, v(-1.74, 42.3) * mm, v(0, 42.3) * mm, v(1.36, 42.3) * mm, v(3.16, 42.3) * mm, v(3.16, 41.18) * mm, v(1.6, 41.18) * mm, v(-1.27, 40.82) * mm, v(-1.5, 40.22) * mm, v(0, 38.55) * mm, v(1.36, 37.36) * mm, v(3.76, 38.07) * mm, v(6.03, 39.15) * mm, v(6.27, 36.88) * mm, v(4.47, 35.56) * mm, v(2.56, 34.73) * mm, v(0, 34.6) * mm, v(0, 34.85) * mm, v(-2.34, 36.64) * mm, v(-3.18, 38.43) * mm, v(-4.13, 39.63) * mm, v(-6.05, 39.75) * mm, v(-6.64, 36.28) * mm, v(-7.12, 34.6) * mm, v(-7.96, 33.89) * mm, v(-8.08, 35.56) * mm, v(-8.32, 37.36) * mm, v(-9.04, 39.75) * mm, v(-9.75, 40.7) * mm, v(-11.67, 40.22) * mm, v(-12.38, 38.31) * mm, v(-11.9, 36.52) * mm, v(-12.5, 34.49) * mm, v(-13.94, 35.08) * mm, v(-13.94, 37.36) * mm, v(-14.18, 40.22) * mm, v(-14.77, 42.3) * mm, v(-15.37, 44.17) * mm, v(-17.76, 44.17) * mm, v(-19.54, 44.28) * mm]});
            skFitSpline(sketch, "E25", {"points": [v(21, 28.57) * mm, v(20.27, 25.54) * mm, v(20.36, 23.98) * mm, v(20.18, 20.13) * mm, v(20.18, 18.57) * mm, v(20.18, 15.72) * mm, v(22.02, 14.8) * mm, v(23.12, 13.06) * mm, v(24.59, 11.87) * mm, v(27.98, 11.6) * mm, v(30.46, 13.34) * mm, v(33.12, 14.9) * mm, v(33.76, 15.81) * mm, v(34.5, 17.74) * mm, v(33.4, 19.3) * mm, v(33.95, 20.4) * mm, v(35.6, 22.24) * mm, v(35.14, 23.7) * mm, v(34.4, 26.1) * mm, v(32.3, 28.11) * mm, v(28.35, 29.49) * mm, v(26.6, 29.67) * mm, v(23.2, 29.67) * mm, v(21.74, 29.21) * mm, v(21, 28.57) * mm]});
            skFitSpline(sketch, "E26", {"points": [v(-77.73, 15.52) * mm, v(-78.18, 12.17) * mm, v(-78.4, 8.6) * mm, v(-79.74, 6.15) * mm, v(-79.52, 2.8) * mm, v(-79.07, 0) * mm, v(-78.85, -5.23) * mm, v(-78.4, -10.14) * mm, v(-77.95, -14.37) * mm, v(-76.62, -19.06) * mm, v(-75.72, -22.85) * mm, v(-73.94, -27.09) * mm, v(-71.93, -33.11) * mm, v(-71.48, -36.68) * mm, v(-70.37, -40.25) * mm, v(-67.25, -44.71) * mm, v(-65.02, -46.05) * mm, v(-60.55, -50.96) * mm, v(-60.33, -51.4) * mm, v(-56.76, -53.86) * mm, v(-54.3, -57.43) * mm, v(-49.4, -60.77) * mm, v(-44.05, -63.45) * mm, v(-41.6, -64.12) * mm, v(-35.8, -66.35) * mm, v(-27.81, -67.47) * mm, v(-23.52, -68.13) * mm, v(-18.33, -69.03) * mm, v(-11.26, -69.25) * mm, v(-5.23, -68.58) * mm, v(0, -66.73) * mm, v(5.25, -66.73) * mm, v(10.83, -66.73) * mm, v(13.97, -65.05) * mm, v(16.52, -64.24) * mm, v(17.84, -63.13) * mm, v(20.3, -63.13) * mm, v(22.5, -61.7) * mm, v(24.08, -60.81) * mm, v(25.92, -59.93) * mm, v(28.2, -59.85) * mm, v(29.8, -57.47) * mm, v(32.16, -56.5) * mm, v(33.57, -54.48) * mm, v(35.49, -52.81) * mm, v(36.96, -51.64) * mm, v(38.33, -50.46) * mm, v(40.59, -48.8) * mm, v(41.57, -47.32) * mm, v(42.84, -45.56) * mm, v(43.23, -44.48) * mm, v(44.6, -44.18) * mm, v(45.4, -42.61) * mm, v(47.55, -39.28) * mm, v(47.55, -38.5) * mm, v(48.92, -36.43) * mm, v(48.92, -35.26) * mm, v(48.24, -34.87) * mm, v(48.83, -33.4) * mm, v(50.79, -30.35) * mm, v(50.79, -28.88) * mm, v(50.79, -26.33) * mm, v(52.16, -24.57) * mm, v(53.53, -21.72) * mm, v(54.9, -17.9) * mm, v(55.6, -15.15) * mm, v(57.1, -3.86) * mm, v(57.1, 0) * mm, v(57.4, 2.24) * mm, v(57.4, 8.04) * mm, v(57.25, 12.83) * mm, v(55.07, 17.61) * mm, v(55.07, 20.08) * mm, v(54.06, 22.25) * mm, v(53.77, 25.6) * mm, v(52.32, 29.36) * mm, v(50.72, 31.97) * mm, v(51.01, 34.58) * mm, v(48.25, 35.02) * mm, v(46.93, 37.06) * mm, v(45.9, 41.05) * mm, v(44.42, 41.33) * mm, v(41.91, 44.03) * mm, v(39.84, 46.35) * mm, v(37.74, 47) * mm, v(35.79, 50.34) * mm, v(33.1, 52.1) * mm, v(30.77, 54.8) * mm, v(27.99, 55.91) * mm, v(25.02, 56.93) * mm, v(21.3, 58.88) * mm, v(18.05, 61.1) * mm, v(13.6, 62.41) * mm, v(9.81, 63.58) * mm, v(7.06, 65.76) * mm, v(5.54, 65.1) * mm, v(0.81, 65) * mm, v(-2.4, 65.2) * mm, v(-6.48, 65.48) * mm, v(-10.27, 66.14) * mm, v(-13.12, 67.37) * mm, v(-15.1, 67.47) * mm, v(-15.3, 68.88) * mm, v(-19.37, 68.88) * mm, v(-23.54, 68.13) * mm, v(-25.53, 63.96) * mm, v(-27.81, 63.87) * mm, v(-30.26, 63.87) * mm, v(-32.06, 62.41) * mm, v(-34.9, 62.41) * mm, v(-37.46, 62.41) * mm, v(-38.63, 61.01) * mm, v(-39.55, 61.01) * mm, v(-42.58, 59.22) * mm, v(-43.53, 58.75) * mm, v(-45.32, 58.23) * mm, v(-47.24, 56.61) * mm, v(-48.76, 55.6) * mm, v(-50.38, 55.3) * mm, v(-52.7, 53.07) * mm, v(-56.14, 50.04) * mm, v(-57.66, 48.02) * mm, v(-59.48, 46.2) * mm, v(-61.5, 44.38) * mm, v(-61.8, 42.3) * mm, v(-64.63, 41.66) * mm, v(-65.44, 38.92) * mm, v(-67.77, 37) * mm, v(-70.3, 32.25) * mm, v(-72.52, 28.9) * mm, v(-73.94, 26.68) * mm, v(-75.25, 22.94) * mm, v(-76.67, 18.5) * mm, v(-77.73, 15.52) * mm]});
            skSolve(sketch);
        }
        {
            var Q0;
            Q0=qSketchRegion(id+"F0",true);
            extrude(context, id + "F1", {"entities" : qUnion([Q0]), "depth" : 25.4 * mm});
        }
    });
